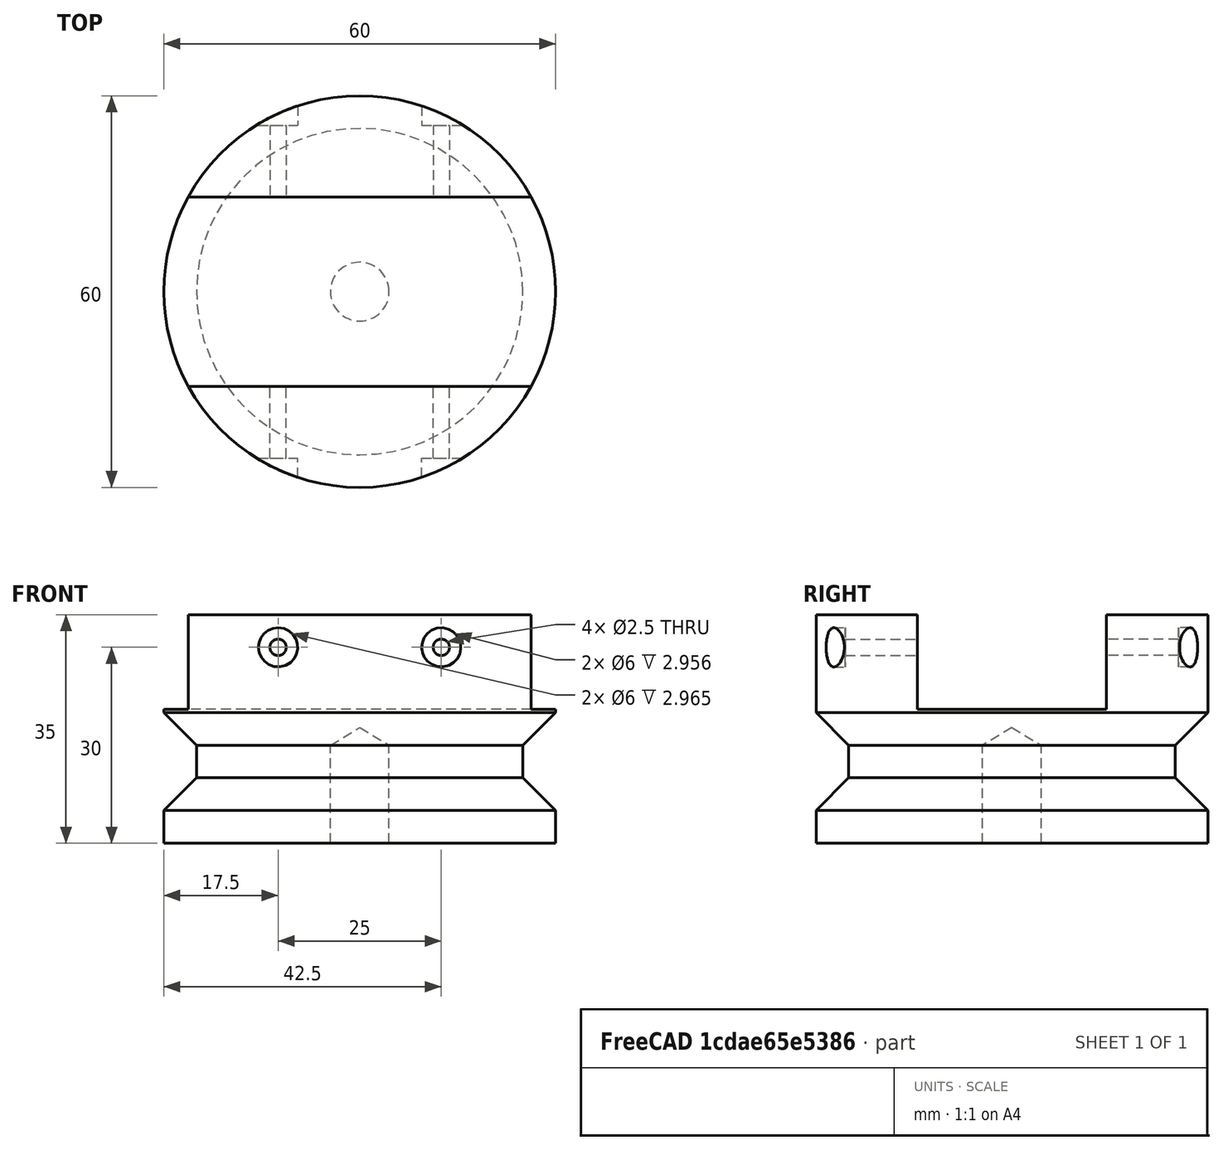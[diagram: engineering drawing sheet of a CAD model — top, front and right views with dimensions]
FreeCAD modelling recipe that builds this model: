
FCSTD DOCUMENT  (FreeCAD 0.21R33771 (Git))
Label: Holder
License: All rights reserved
LicenseURL: http://en.wikipedia.org/wiki/All_rights_reserved
objects: TechDraw::DrawViewDimension×12, Sketcher::SketchObject×4, TechDraw::DrawProjGroupItem×4, PartDesign::Hole×2, PartDesign::CoordinateSystem×2, PartDesign::Revolution×1, TechDraw::DrawSVGTemplate×1, TechDraw::DrawProjGroup×1, TechDraw::DrawViewSection×1, PartDesign::Pocket×1, PartDesign::Mirrored×1, PartDesign::Body×1, TechDraw::DrawViewPart×1, TechDraw::DrawPage×1
note: 16 computed .brp shape members not serialized (recipe doc carries the construction recipe); baked Part::Feature solids carry a one-line shape summary decoded from their .brp

FEATURE [Sketcher::SketchObject] Sketch  label="cone"
  FullyConstrained = true
  MapMode = 5
  Placement = pos=(0,0,0) rot=(0.57735,0.57735,0.57735;2.0944rad)
  Support = -> [YZ_Plane]
  sketch-geometry (8):
    g0: LineSegment StartX=0 StartY=0 StartZ=0 EndX=0 EndY=35 EndZ=0
    g1: LineSegment StartX=0 StartY=35 StartZ=0 EndX=-30 EndY=35 EndZ=0
    g2: LineSegment StartX=-30 StartY=0 StartZ=0 EndX=0 EndY=0 EndZ=0
    g3: LineSegment StartX=-30 StartY=35 StartZ=0 EndX=-30 EndY=20 EndZ=0
    g4: LineSegment StartX=-30 StartY=20 StartZ=0 EndX=-25 EndY=15 EndZ=0
    g5: LineSegment StartX=-25 StartY=15 StartZ=0 EndX=-25 EndY=10 EndZ=0
    g6: LineSegment StartX=-25 StartY=10 StartZ=0 EndX=-30 EndY=5 EndZ=0
    g7: LineSegment StartX=-30 StartY=5 StartZ=0 EndX=-30 EndY=0 EndZ=0
  constraints (23):
    c: PointOnObject(g0,g-2)
    c: Coincident(g0,g1)
    c: Horizontal(g1)
    c: DistanceY(g-1,g0) = 35  'height'
    c: Coincident(g0,g-1)
    c: Coincident(g2,g0)
    c: Horizontal(g2)
    c: DistanceX(g1,g1) = 30  'width'
    c: Coincident(g1,g3)
    c: Vertical(g3)
    c: Coincident(g3,g4)
    c: Coincident(g4,g5)
    c: Vertical(g5)
    c: Coincident(g5,g6)
    c: Coincident(g6,g7)
    c: Coincident(g7,g2)
    c: Vertical(g7)
    c: Angle(g7,g6) = 2.35619
    c: Angle(g4,g3) = 2.35619
    c: Vertical(g6,g3)
    c: DistanceY(g7,g7) = 5
    c: DistanceY(g5,g5) = 5
    c: DistanceY(g3,g3) = 15
FEATURE [PartDesign::Revolution] Revolution  label="Cone"
  Angle = 360
  Axis = (-2e-16,3e-16,1)
  Base = (0,0,0)
  Profile = -> Sketch
  ReferenceAxis = -> Sketch [V_Axis]
FEATURE [Sketcher::SketchObject] Sketch001  label="slot"
  FullyConstrained = true
  MapMode = 5
  Placement = pos=(0,0,0) rot=(0.57735,0.57735,0.57735;2.0944rad)
  Support = -> [YZ_Plane]
  expr: Constraints[10] = <<cone>>.Constraints.height
  sketch-geometry (4):
    g0: LineSegment StartX=14.5 StartY=35 StartZ=0 EndX=14.5 EndY=20.5 EndZ=0
    g1: LineSegment StartX=14.5 StartY=20.5 StartZ=0 EndX=-14.5 EndY=20.5 EndZ=0
    g2: LineSegment StartX=-14.5 StartY=20.5 StartZ=0 EndX=-14.5 EndY=35 EndZ=0
    g3: LineSegment StartX=-14.5 StartY=35 StartZ=0 EndX=14.5 EndY=35 EndZ=0
  constraints (11):
    c: Vertical(g0)
    c: Coincident(g0,g1)
    c: Horizontal(g1)
    c: Coincident(g1,g2)
    c: Vertical(g2)
    c: Symmetric(g2,g0,g-2)
    c: DistanceX(g1,g1) = 29  'width'
    c: Coincident(g3,g2)
    c: Coincident(g3,g0)
    c: DistanceY(g0,g0) = 14.5
    c: DistanceY(g-1,g0) = 35
FEATURE [Sketcher::SketchObject] Sketch002  label="hole"
  AttachmentOffset = pos=(0,0,30) rot=(0,0,1;0rad)
  FullyConstrained = true
  MapMode = 5
  Placement = pos=(0,-30,-6.7e-15) rot=(1,0,0;1.5708rad)
  Support = -> [XZ_Plane]
  expr: .AttachmentOffset.Base.z = Sketch.Constraints.width
  expr: Constraints[1] = <<cone>>.Constraints.height - 5 mm
  sketch-geometry (2):
    g0: Circle CenterX=-12.5 CenterY=30 CenterZ=0 NormalX=0 NormalY=0 NormalZ=1 AngleXU=0 Radius=1.25
    g1: Circle CenterX=12.5 CenterY=30 CenterZ=0 NormalX=0 NormalY=0 NormalZ=1 AngleXU=0 Radius=1.25
  constraints (5):
    c: Diameter(g0) = 2.5
    c: DistanceY(g-1,g0) = 30
    c: Equal(g1,g0)
    c: Symmetric(g1,g0,g-2)
    c: DistanceX(g0,g1) = 25
FEATURE [Sketcher::SketchObject] Sketch003  label="thread"
  FullyConstrained = true
  MapMode = 5
  Support = -> [XY_Plane]
  sketch-geometry (1):
    g0: Circle CenterX=0 CenterY=0 CenterZ=0 NormalX=0 NormalY=0 NormalZ=1 AngleXU=0 Radius=3.5
  constraints (2):
    c: Coincident(g0,g-1)
    c: Diameter(g0) = 7
FEATURE [TechDraw::DrawSVGTemplate] Template
  Height = 297
  Orientation = 1
  Width = 420
FEATURE [TechDraw::DrawProjGroupItem] ProjItem  label="Front"
  CoarseView = false
  Direction = (-1,0,0)
  Focus = 100
  HardHidden = false
  IsoCount = 0
  IsoHidden = false
  IsoVisible = false
  LockPosition = true
  Perspective = false
  Rotation = 0
  RotationVector = (0,-1,0)
  ScaleType = 2
  ScrubCount = 0
  SeamHidden = false
  SeamVisible = true
  SmoothHidden = false
  SmoothVisible = true
  Type = 0
  X = 0
  XDirection = (0,-1,0)
  Y = 0
FEATURE [TechDraw::DrawProjGroupItem] ProjItem003  label="Top"
  CoarseView = false
  Direction = (0,0,1)
  Focus = 100
  HardHidden = true
  IsoCount = 0
  IsoHidden = false
  IsoVisible = false
  LockPosition = false
  Perspective = false
  Rotation = 0
  RotationVector = (1,0,0)
  ScaleType = 2
  ScrubCount = 0
  SeamHidden = false
  SeamVisible = true
  SmoothHidden = false
  SmoothVisible = true
  Type = 4
  X = 0
  XDirection = (0,-1,0)
  Y = 85.7124
FEATURE [TechDraw::DrawProjGroupItem] ProjItem002  label="Bottom"
  CoarseView = false
  Direction = (0,0,-1)
  Focus = 100
  HardHidden = false
  IsoCount = 0
  IsoHidden = false
  IsoVisible = false
  LockPosition = false
  Perspective = false
  Rotation = 0
  RotationVector = (1,0,0)
  ScaleType = 2
  ScrubCount = 0
  SeamHidden = false
  SeamVisible = true
  SmoothHidden = false
  SmoothVisible = true
  Type = 5
  X = 0
  XDirection = (0,-1,0)
  Y = -79.9093
FEATURE [TechDraw::DrawViewDimension] Dimension004
  AngleOverride = false
  Arbitrary = true
  ArbitraryTolerances = false
  EqualTolerance = true
  ExtensionAngle = 0
  FormatSpec = M8 ↧15
  FormatSpecOverTolerance = %+.2w
  FormatSpecUnderTolerance = %+.2w
  Inverted = false
  LineAngle = 0
  LockPosition = false
  MeasureType = 1
  OverTolerance = 0
  References2D = -> [ProjItem002]
  Rotation = 0
  ScaleType = 0
  TheoreticalExact = false
  Type = 5
  UnderTolerance = 0
  X = -63.7982
  Y = 30.8498
FEATURE [TechDraw::DrawViewDimension] Dimension
  AngleOverride = false
  Arbitrary = false
  ArbitraryTolerances = false
  EqualTolerance = true
  ExtensionAngle = 0
  FormatSpec = ⌀%.2w
  FormatSpecOverTolerance = %+.2w
  FormatSpecUnderTolerance = %+.2w
  Inverted = false
  LineAngle = 0
  LockPosition = false
  MeasureType = 1
  OverTolerance = 0
  References2D = -> [ProjItem002]
  Rotation = 0
  ScaleType = 0
  TheoreticalExact = false
  Type = 5
  UnderTolerance = 0
  X = -70.3298
  Y = -13.9289
FEATURE [TechDraw::DrawProjGroupItem] ProjItem004  label="Right"
  CoarseView = false
  Direction = (-1e-16,-1,0)
  Focus = 100
  HardHidden = false
  IsoCount = 0
  IsoHidden = false
  IsoVisible = true
  LockPosition = false
  Perspective = false
  Rotation = 0
  RotationVector = (1,0,0)
  ScaleType = 2
  ScrubCount = 0
  SeamHidden = false
  SeamVisible = false
  SmoothHidden = false
  SmoothVisible = true
  Type = 2
  X = 110.789
  XDirection = (1,-1e-16,0)
  Y = 0
FEATURE [TechDraw::DrawProjGroup] ProjGroup
  Anchor = -> ProjItem
  AutoDistribute = false
  LockPosition = false
  ProjectionType = 1
  Rotation = 0
  ScaleType = 0
  Views = -> [ProjItem,ProjItem002,ProjItem003,ProjItem004]
  X = 124.891
  Y = 143.381
  spacingX = 15
  spacingY = 15
FEATURE [TechDraw::DrawViewDimension] Dimension011
  AngleOverride = false
  Arbitrary = false
  ArbitraryTolerances = false
  EqualTolerance = true
  ExtensionAngle = 0
  FormatSpec = %.2w
  FormatSpecOverTolerance = %+.2w
  FormatSpecUnderTolerance = %+.2w
  Inverted = false
  LineAngle = 0
  LockPosition = false
  MeasureType = 1
  OverTolerance = 0
  References2D = -> [ProjItem004]
  Rotation = 0
  ScaleType = 0
  TheoreticalExact = false
  Type = 1
  UnderTolerance = 0
  X = -28.2589
  Y = 35.4152
FEATURE [TechDraw::DrawViewDimension] Dimension009
  AngleOverride = false
  Arbitrary = false
  ArbitraryTolerances = false
  EqualTolerance = true
  ExtensionAngle = 0
  FormatSpec = 4X ⌀%.2w THRU ⌴⌀6↧4.5
  FormatSpecOverTolerance = %+.2w
  FormatSpecUnderTolerance = %+.2w
  Inverted = false
  LineAngle = 0
  LockPosition = false
  MeasureType = 1
  OverTolerance = 0
  References2D = -> [ProjItem004]
  Rotation = 0
  ScaleType = 0
  TheoreticalExact = false
  Type = 5
  UnderTolerance = 0
  X = 72.9187
  Y = -1.0129
FEATURE [TechDraw::DrawViewSection] SectionView  label="Section A - A"
  BaseView = -> ProjItem003
  CoarseView = false
  CutSurfaceDisplay = 2
  Direction = (-1,-1e-16,0)
  FileGeomPattern = <path>
  FileHatchPattern = <path>
  Focus = 100
  FuseBeforeCut = false
  HardHidden = false
  HatchOffset = (0,0,0)
  HatchRotation = 0
  HatchScale = 1
  IsoCount = 0
  IsoHidden = false
  IsoVisible = true
  LockPosition = false
  NameGeomPattern = Diamond
  Perspective = false
  Rotation = 0
  ScaleType = 2
  ScrubCount = 0
  SeamHidden = false
  SeamVisible = true
  SectionDirection = 0
  SectionNormal = (-1,-1e-16,0)
  SectionOrigin = (0,0,17.51)
  SectionSymbol = A
  SmoothHidden = false
  SmoothVisible = true
  TrimAfterCut = false
  X = 236.253
  XDirection = (1e-16,-1,0)
  Y = 220.836
FEATURE [TechDraw::DrawViewDimension] Dimension007
  AngleOverride = false
  Arbitrary = false
  ArbitraryTolerances = false
  EqualTolerance = true
  ExtensionAngle = 0
  FormatSpec = %.2w
  FormatSpecOverTolerance = %+.2w
  FormatSpecUnderTolerance = %+.2w
  Inverted = false
  LineAngle = 0
  LockPosition = false
  MeasureType = 1
  OverTolerance = 0
  References2D = -> [SectionView]
  Rotation = 0
  ScaleType = 0
  TheoreticalExact = false
  Type = 6
  UnderTolerance = 0
  X = 47.7226
  Y = -6.41254
FEATURE [TechDraw::DrawViewDimension] Dimension010
  AngleOverride = false
  Arbitrary = false
  ArbitraryTolerances = false
  EqualTolerance = true
  ExtensionAngle = 0
  FormatSpec = %.2w
  FormatSpecOverTolerance = %+.2w
  FormatSpecUnderTolerance = %+.2w
  Inverted = false
  LineAngle = 0
  LockPosition = false
  MeasureType = 1
  OverTolerance = 0
  References2D = -> [SectionView]
  Rotation = 0
  ScaleType = 0
  TheoreticalExact = false
  Type = 1
  UnderTolerance = 0
  X = 0.247712
  Y = 49.9322
FEATURE [TechDraw::DrawViewDimension] Dimension006
  AngleOverride = false
  Arbitrary = false
  ArbitraryTolerances = false
  EqualTolerance = true
  ExtensionAngle = 0
  FormatSpec = %.2w
  FormatSpecOverTolerance = %+.2w
  FormatSpecUnderTolerance = %+.2w
  Inverted = false
  LineAngle = 0
  LockPosition = false
  MeasureType = 1
  OverTolerance = 0
  References2D = -> [Dimension007,SectionView]
  Rotation = 0
  ScaleType = 0
  TheoreticalExact = false
  Type = 2
  UnderTolerance = 0
  X = -49.0556
  Y = 34.2523
FEATURE [TechDraw::DrawViewDimension] Dimension005
  AngleOverride = false
  Arbitrary = false
  ArbitraryTolerances = false
  EqualTolerance = true
  ExtensionAngle = 0
  FormatSpec = %.2w
  FormatSpecOverTolerance = %+.2w
  FormatSpecUnderTolerance = %+.2w
  Inverted = false
  LineAngle = 0
  LockPosition = false
  MeasureType = 1
  OverTolerance = 0
  References2D = -> [SectionView]
  Rotation = 0
  ScaleType = 0
  TheoreticalExact = false
  Type = 1
  UnderTolerance = 0
  X = 0.190286
  Y = 36.7069
FEATURE [TechDraw::DrawViewDimension] Dimension013
  AngleOverride = false
  Arbitrary = false
  ArbitraryTolerances = false
  EqualTolerance = true
  ExtensionAngle = 0
  FormatSpec = %.2w
  FormatSpecOverTolerance = %+.2w
  FormatSpecUnderTolerance = %+.2w
  Inverted = false
  LineAngle = 0
  LockPosition = false
  MeasureType = 1
  OverTolerance = 0
  References2D = -> [ProjItem]
  Rotation = 0
  ScaleType = 0
  TheoreticalExact = false
  Type = 2
  UnderTolerance = 0
  X = -66.3225
  Y = 1.97021
FEATURE [TechDraw::DrawViewDimension] Dimension014
  AngleOverride = false
  Arbitrary = false
  ArbitraryTolerances = false
  EqualTolerance = true
  ExtensionAngle = 0
  FormatSpec = %.2w
  FormatSpecOverTolerance = %+.2w
  FormatSpecUnderTolerance = %+.2w
  Inverted = false
  LineAngle = 0
  LockPosition = false
  MeasureType = 1
  OverTolerance = 0
  References2D = -> [ProjItem004]
  Rotation = 0
  ScaleType = 0
  TheoreticalExact = false
  Type = 2
  UnderTolerance = 0
  X = -46.9361
  Y = -1.01148
FEATURE [TechDraw::DrawViewDimension] Dimension015
  AngleOverride = false
  Arbitrary = false
  ArbitraryTolerances = false
  EqualTolerance = true
  ExtensionAngle = 0
  FormatSpec = %.2w
  FormatSpecOverTolerance = %+.2w
  FormatSpecUnderTolerance = %+.2w
  Inverted = false
  LineAngle = 0
  LockPosition = false
  MeasureType = 1
  OverTolerance = 0
  References2D = -> [ProjItem]
  Rotation = 0
  ScaleType = 0
  TheoreticalExact = false
  Type = 2
  UnderTolerance = 0
  X = -42.7174
  Y = -28.1212
FEATURE [TechDraw::DrawViewDimension] Dimension016
  AngleOverride = false
  Arbitrary = false
  ArbitraryTolerances = false
  EqualTolerance = true
  ExtensionAngle = 0
  FormatSpec = %.2w
  FormatSpecOverTolerance = %+.2w
  FormatSpecUnderTolerance = %+.2w
  Inverted = false
  LineAngle = 0
  LockPosition = false
  MeasureType = 1
  OverTolerance = 0
  References2D = -> [ProjItem]
  Rotation = 0
  ScaleType = 0
  TheoreticalExact = false
  Type = 2
  UnderTolerance = 0
  X = -52.9399
  Y = -28.141
FEATURE [PartDesign::Pocket] Pocket
  BaseFeature = -> Revolution
  Direction = (-1,2e-16,-3e-16)
  Length = 5
  Length2 = 5
  Midplane = true
  Profile = -> Sketch001
  ReferenceAxis = -> Sketch001 [N_Axis]
  Type = 1
FEATURE [PartDesign::Hole] Hole
  BaseFeature = -> Pocket
  CustomThreadClearance = 0
  Depth = 30
  DepthType = 0
  Diameter = 2.5
  DrillForDepth = false
  DrillPoint = 1
  DrillPointAngle = 118
  HoleCutCountersinkAngle = 90
  HoleCutCustomValues = false
  HoleCutDepth = 4.5
  HoleCutDiameter = 6
  HoleCutType = 1
  ModelThread = false
  Profile = -> Sketch002 [Edge1,Edge2]
  Tapered = false
  TaperedAngle = 90
  ThreadClass = 0
  ThreadDepth = 30
  ThreadDepthType = 0
  ThreadDirection = 0
  ThreadFit = 0
  ThreadSize = 9
  ThreadType = 1
  Threaded = true
  UseCustomThreadClearance = false
  expr: Depth = Sketch.Constraints.width
FEATURE [PartDesign::Mirrored] Mirrored
  BaseFeature = -> Hole
  MirrorPlane = -> XZ_Plane
  Originals = -> [Hole]
FEATURE [PartDesign::Hole] Hole001
  BaseFeature = -> Mirrored
  CustomThreadClearance = 0
  Depth = 15
  DepthType = 0
  Diameter = 9
  DrillForDepth = false
  DrillPoint = 1
  DrillPointAngle = 118
  HoleCutCountersinkAngle = 90
  HoleCutCustomValues = false
  HoleCutDepth = 0
  HoleCutDiameter = 6.1
  HoleCutType = 0
  ModelThread = false
  Profile = -> Sketch003
  Reversed = true
  Tapered = false
  TaperedAngle = 90
  ThreadClass = 0
  ThreadDepth = 15
  ThreadDepthType = 0
  ThreadDirection = 0
  ThreadFit = 0
  ThreadSize = 16
  ThreadType = 1
  Threaded = false
  UseCustomThreadClearance = false
FEATURE [PartDesign::CoordinateSystem] Local_CS
  AttacherType = Attacher::AttachEngine3D
  MapMode = 11
  Placement = pos=(0,0,0) rot=(0.707107,0.707107,0;3.14159rad)
  Support = -> [Hole001]
FEATURE [PartDesign::CoordinateSystem] Local_CS001
  AttacherType = Attacher::AttachEngine3D
  MapMode = 45
  Placement = pos=(1.3e-15,4.8e-15,20.5) rot=(0,0,1;1.5708rad)
  Support = -> [Hole001]
FEATURE [PartDesign::Body] Body  label="Holder"
  Group = -> [Sketch,Revolution,Sketch001,Sketch002,Pocket,Hole,Sketch003,Mirrored,Local_CS,Local_CS001,Hole001]
  Origin = -> Origin
  Tip = -> Hole001
FEATURE [TechDraw::DrawViewPart] View  label="Iso"
  CoarseView = false
  Direction = (-0.577,-0.577,0.577)
  Focus = 100
  HardHidden = false
  IsoCount = 0
  IsoHidden = false
  IsoVisible = false
  LockPosition = false
  Perspective = false
  Rotation = 0
  ScaleType = 0
  ScrubCount = 0
  SeamHidden = false
  SeamVisible = false
  SmoothHidden = false
  SmoothVisible = true
  Source = -> [Body]
  X = 350.974
  XDirection = (0.707,-0.707,0)
  Y = 218.276
FEATURE [TechDraw::DrawPage] Page
  KeepUpdated = true
  NextBalloonIndex = 1
  ProjectionType = 0
  Template = -> Template
  Views = -> [ProjGroup,View,Dimension004,SectionView,Dimension,Dimension005,Dimension006,Dimension007,Dimension009,Dimension010,Dimension011,Dimension013,Dimension014,Dimension015,Dimension016]
note: 2 file-system paths scrubbed to <path> (originals preserved in the JSON sidecar)
